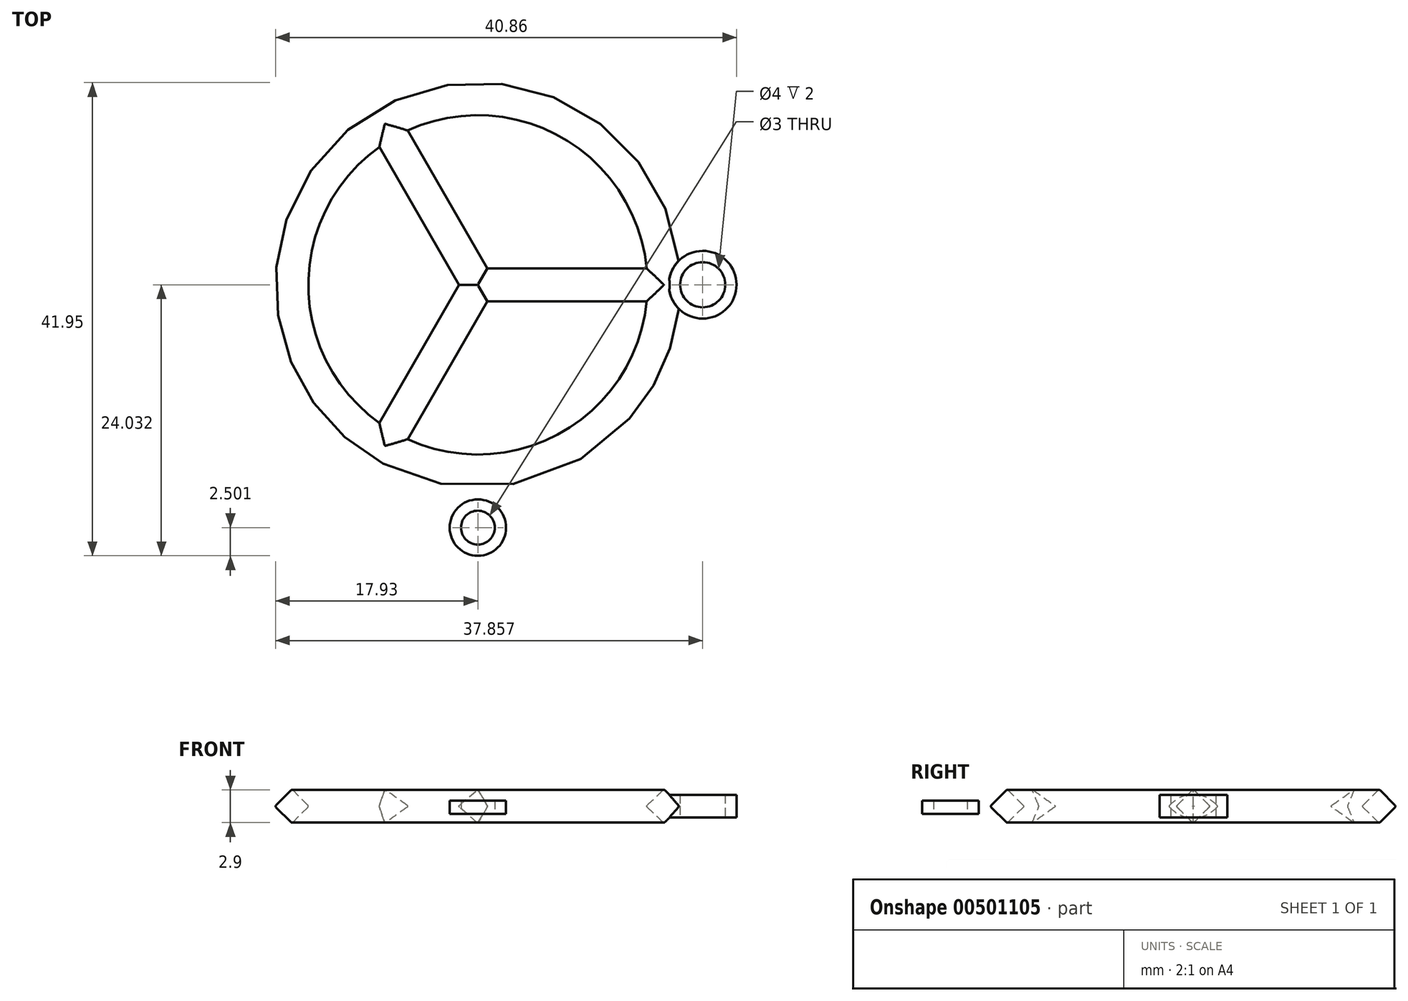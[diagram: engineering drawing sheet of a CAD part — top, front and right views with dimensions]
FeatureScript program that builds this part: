
annotation { "Feature Type Name" : "Feature", "Feature Type Description" : "" }
export const myFeature = defineFeature(function(context is Context, id is Id, definition is map)
    precondition{}
    {
        {
            var Q0;
            Q0=qCreatedBy(makeId("Front.planeOp"),FACE);
            var sketch = newSketch(context, id + "F0", { "sketchPlane" : qUnion([Q0])});
            skLineSegment(sketch, "E0", {"start": v(0, 0) * mm, "end": v(-16.5, 0) * mm});
            skLineSegment(sketch, "E1", {"start": v(0, 0) * mm, "end": v(16.5, 0) * mm});
            skCircle(sketch, "E2", {"center": v(16.5, 0) * mm, "radius": 1.5 * mm});
            skCircle(sketch, "E3", {"center": v(-16.48, 0) * mm, "radius": 1.5 * mm});
            skCircle(sketch, "E4.cCircle", {"center": v(-16.48, 0) * mm, "radius": 1.5 * mm, "construction": true});
            skLineSegment(sketch, "E4.0", {"start": v(-15.07, -0.1) * mm, "end": v(-16.4, -1.4) * mm});
            skLineSegment(sketch, "E4.1", {"start": v(-16.57, -1.4) * mm, "end": v(-17.9, -0.1) * mm});
            skLineSegment(sketch, "E4.2", {"start": v(-17.9, 0.1) * mm, "end": v(-16.57, 1.4) * mm});
            skLineSegment(sketch, "E4.3", {"start": v(-16.4, 1.4) * mm, "end": v(-15.07, 0.1) * mm});
            skPoint(sketch, "E5.visualSharp", {"position": v(-14.98, 0) * mm});
            skArc(sketch, "E5.filletArc", {"start": v(-15.07, -0.1) * mm, "mid": v(-15.04, 0) * mm, "end": v(-15.07, 0.1) * mm});
            skPoint(sketch, "E6.visualSharp", {"position": v(-16.48, 1.5) * mm});
            skArc(sketch, "E6.filletArc", {"start": v(-16.4, 1.4) * mm, "mid": v(-16.48, 1.45) * mm, "end": v(-16.57, 1.4) * mm});
            skPoint(sketch, "E7.visualSharp", {"position": v(-17.98, 0) * mm});
            skArc(sketch, "E7.filletArc", {"start": v(-17.9, 0.1) * mm, "mid": v(-17.93, 0) * mm, "end": v(-17.9, -0.1) * mm});
            skPoint(sketch, "E8.visualSharp", {"position": v(-16.48, -1.5) * mm});
            skArc(sketch, "E8.filletArc", {"start": v(-16.57, -1.4) * mm, "mid": v(-16.48, -1.45) * mm, "end": v(-16.4, -1.4) * mm});
            skSolve(sketch);
        }
        {
            var Q0;
            Q0=qCreatedBy(makeId("Front.planeOp"),FACE);
            var sketch = newSketch(context, id + "F1", { "sketchPlane" : qUnion([Q0])});
            skLineSegment(sketch, "E9", {"start": v(0, 51.47) * mm, "end": v(0, -44.85) * mm});
            skSolve(sketch);
        }
        {
            var Q0;
            {var subQ1=sQuery(id+"F0.wireOp",EDGE,"E4.0");Q0=makeQuery(id+"F0.imprint","IMPRINT",FACE,{"disambiguationData":[TD([[makeQuery(id+"F0.imprint","IMPRINT",EDGE,{"derivedFrom":subQ1}),-1.0]])]});}
            var Q1;
            Q1=sQuery(id+"F1.wireOp",EDGE,"E9");
            revolve(context, id + "F2", {"entities" : qUnion([Q0]), "axis" : qUnion([Q1]), "revolveType" : RevolveType.FULL});
        }
        {
            var Q0;
            Q0=qCreatedBy(makeId("Right.planeOp"),FACE);
            var sketch = newSketch(context, id + "F3", { "sketchPlane" : qUnion([Q0])});
            skLineSegment(sketch, "E10.0", {"start": v(1.4, -0.1) * mm, "end": v(0.1, -1.4) * mm});
            skLineSegment(sketch, "E10.1", {"start": v(-0.1, -1.4) * mm, "end": v(-1.4, -0.1) * mm});
            skLineSegment(sketch, "E10.2", {"start": v(-1.4, 0.1) * mm, "end": v(-0.1, 1.4) * mm});
            skLineSegment(sketch, "E10.3", {"start": v(0.1, 1.4) * mm, "end": v(1.4, 0.1) * mm});
            skArc(sketch, "E11.filletArc", {"start": v(1.4, -0.1) * mm, "mid": v(1.45, 0) * mm, "end": v(1.4, 0.1) * mm});
            skArc(sketch, "E12.filletArc", {"start": v(0.1, 1.4) * mm, "mid": v(0, 1.45) * mm, "end": v(-0.1, 1.4) * mm});
            skArc(sketch, "E13.filletArc", {"start": v(-1.4, 0.1) * mm, "mid": v(-1.45, 0) * mm, "end": v(-1.4, -0.1) * mm});
            skArc(sketch, "E14.filletArc", {"start": v(-0.1, -1.4) * mm, "mid": v(0, -1.45) * mm, "end": v(0.1, -1.4) * mm});
            skSolve(sketch);
        }
        {
            var Q0;
            Q0=makeQuery(id+"F3.imprint","IMPRINT",FACE,{"disambiguationData":[TD([[makeQuery(id+"F3.imprint","IMPRINT",EDGE,{"derivedFrom":sQuery(id+"F3.wireOp",EDGE,"E10.0")}),-1.0]])]});
            extrude(context, id + "F4", {"entities" : qUnion([Q0]), "operationType" : NewBodyOperationType.ADD, "depth" : 16.48 * mm});
        }
        {
            var Q0;
            Q0=qCreatedBy(makeId("Top.planeOp"),FACE);
            var sketch = newSketch(context, id + "F5", { "sketchPlane" : qUnion([Q0])});
            skCircle(sketch, "E15", {"center": v(0, -21.52) * mm, "radius": 1.5 * mm});
            skCircle(sketch, "E16", {"center": v(0, -21.52) * mm, "radius": 2.5 * mm});
            skSolve(sketch);
        }
        {
            var Q0;
            Q0=makeQuery(id+"F5.imprint","IMPRINT",FACE,{"disambiguationData":[TD([[makeQuery(id+"F5.imprint","IMPRINT",EDGE,{"derivedFrom":sQuery(id+"F5.wireOp",EDGE,"E15")}),-1.0]])]});
            var Q1;
            Q1=sQuery(id+"F5.wireOp",EDGE,"E15");
            var Q2;
            Q2=sQuery(id+"F5.wireOp",EDGE,"E16");
            extrude(context, id + "F6", {"entities" : qUnion([Q0]), "operationType" : NewBodyOperationType.ADD, "surfaceEntities" : qUnion([Q1, Q2]), "depth" : 0.5 * mm, "hasSecondDirection" : true, "secondDirectionOppositeDirection" : true, "secondDirectionDepth" : 0.68 * mm});
        }
        {
            var Q0;
            Q0=makeQuery(id+"F2.opRevolve","SWEPT_BODY",BODY,{"disambiguationData":[OSD([sQuery(id+"F0.wireOp",EDGE,"E4.0"),sQuery(id+"F0.wireOp",EDGE,"E4.1"),sQuery(id+"F0.wireOp",EDGE,"E4.2"),sQuery(id+"F0.wireOp",EDGE,"E4.3"),sQuery(id+"F0.wireOp",EDGE,"E5.filletArc"),sQuery(id+"F0.wireOp",EDGE,"E6.filletArc"),sQuery(id+"F0.wireOp",EDGE,"E7.filletArc"),sQuery(id+"F0.wireOp",EDGE,"E8.filletArc")])]});
            var Q1;
            Q1=sQuery(id+"F1.wireOp",EDGE,"E9");
            var Q2;
            Q2=sQuery(id+"F1.wireOp",EDGE,"E9");
            transform(context, id + "F7", {"entities" : qUnion([Q0]), "transformType" : TransformType.ROTATION, "transformAxis" : qUnion([Q2]), "angle" : 120 * degree, "makeCopy" : true});
        }
        {
            var Q0;
            Q0=makeQuery(id+"F2.opRevolve","SWEPT_BODY",BODY,{"disambiguationData":[OSD([sQuery(id+"F0.wireOp",EDGE,"E4.0"),sQuery(id+"F0.wireOp",EDGE,"E4.1"),sQuery(id+"F0.wireOp",EDGE,"E4.2"),sQuery(id+"F0.wireOp",EDGE,"E4.3"),sQuery(id+"F0.wireOp",EDGE,"E5.filletArc"),sQuery(id+"F0.wireOp",EDGE,"E6.filletArc"),sQuery(id+"F0.wireOp",EDGE,"E7.filletArc"),sQuery(id+"F0.wireOp",EDGE,"E8.filletArc")])]});
            var Q1;
            Q1=makeQuery(id+"F7.opPattern","COPY",BODY,{"derivedFrom":makeQuery(id+"F2.opRevolve","SWEPT_BODY",BODY,{"disambiguationData":[OSD([sQuery(id+"F0.wireOp",EDGE,"E4.0"),sQuery(id+"F0.wireOp",EDGE,"E4.1"),sQuery(id+"F0.wireOp",EDGE,"E4.2"),sQuery(id+"F0.wireOp",EDGE,"E4.3"),sQuery(id+"F0.wireOp",EDGE,"E5.filletArc"),sQuery(id+"F0.wireOp",EDGE,"E6.filletArc"),sQuery(id+"F0.wireOp",EDGE,"E7.filletArc"),sQuery(id+"F0.wireOp",EDGE,"E8.filletArc")])]}),"instanceName":"1"});
            var Q2;
            Q2=sQuery(id+"F1.wireOp",EDGE,"E9");
            transform(context, id + "F8", {"entities" : qUnion([Q0, Q1]), "transformType" : TransformType.ROTATION, "transformAxis" : qUnion([Q2]), "angle" : 120 * degree, "makeCopy" : true});
        }
        {
            var Q0;
            Q0=qCreatedBy(makeId("Top.planeOp"),FACE);
            var Q1;
            Q1=qCreatedBy(makeId("Top.planeOp"),FACE);
            var sketch = newSketch(context, id + "F9", { "sketchPlane" : qUnion([Q0, Q1])});
            skCircle(sketch, "E17", {"center": v(19.93, 0.01) * mm, "radius": 3 * mm});
            skCircle(sketch, "E18", {"center": v(19.93, 0.01) * mm, "radius": 2 * mm});
            skSolve(sketch);
        }
        {
            var Q0;
            Q0=makeQuery(id+"F9.imprint","IMPRINT",FACE,{"disambiguationData":[TD([[makeQuery(id+"F9.imprint","IMPRINT",EDGE,{"derivedFrom":sQuery(id+"F9.wireOp",EDGE,"E17")}),1.0]])]});
            extrude(context, id + "F10", {"entities" : qUnion([Q0]), "operationType" : NewBodyOperationType.ADD, "depth" : 1 * mm, "hasSecondDirection" : true, "secondDirectionOppositeDirection" : true, "secondDirectionDepth" : 1 * mm});
        }
    });
